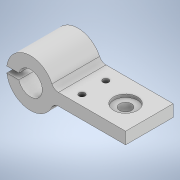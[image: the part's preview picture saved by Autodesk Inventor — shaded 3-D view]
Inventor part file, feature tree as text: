
AUTODESK INVENTOR PART (.ipt)
format: ipt  version: 2022.2 (Build 262287030, 287C)  size: 143,360 bytes
history: native  units: in
note: dims shown in document units (in); Inventor stores cm internally (conversion verified against a paired STEP export)
features: sketch x3, hole x2, extrude x1, fillet x1
ambient origin geometry x8: Origin, YZ Plane, XZ Plane, XY Plane, X Axis, Y Axis, Z Axis, Center Point
bodies: Solid1 (feature_tree)
feature tree (7):
  extrude  "Extrusion1"  Depth=0.5in
  hole  "Hole1"  [1 undecoded]
  hole  "Hole2"  [1 undecoded]
  fillet  "Fillet1"  Radius=1.0in
  sketch  "Sketch1"  dims[d0=2.0in d1=0.5in]
  sketch  "Sketch2"  dims[d2=0.25in d3=1.0in]
  sketch  "Sketch3"  dims[d4=4.0in d5=2.0in d6=0.0in d7=1.0in d8=1.0in d9=0.5in d10=0.75in d11=1.0in d12=0.125in d13=0.5635in d14=1.0in d15=0.8108in d16=1.0in d17=2.25in d18=0.25in d19=0.75in d20=1.0in d21=0.125in d22=0.5635in d23=1.0in d24=0.8108in d25=0.3in]
note: 2 required parameter values undecoded (feature->parameter linkage not recoverable at this tier; creation-order binding heuristic only, values carry confidence <= 0.55)
